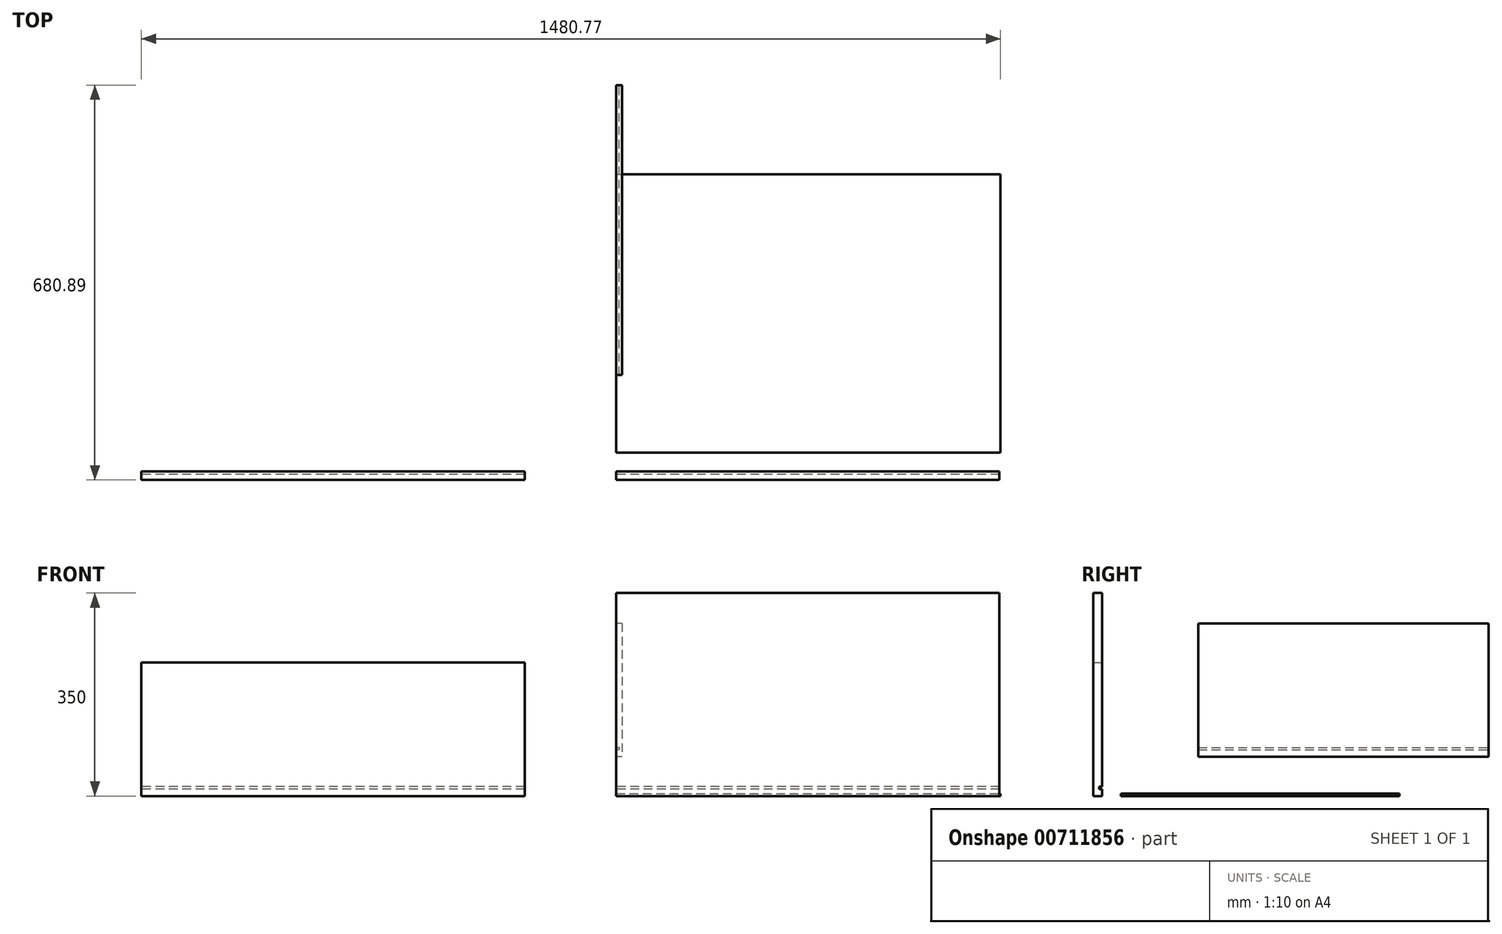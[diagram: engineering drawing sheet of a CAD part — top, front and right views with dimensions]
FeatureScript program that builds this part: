
annotation { "Feature Type Name" : "Feature", "Feature Type Description" : "" }
export const myFeature = defineFeature(function(context is Context, id is Id, definition is map)
    precondition{}
    {
        {
            var Q0;
            Q0=qCreatedBy(makeId("Front.planeOp"),FACE);
            var sketch = newSketch(context, id + "F0", { "sketchPlane" : qUnion([Q0])});
            skLineSegment(sketch, "E0.bottom", {"start": v(0, 0) * mm, "end": v(660.5, 0) * mm});
            skLineSegment(sketch, "E0.top", {"start": v(0, 350) * mm, "end": v(660.5, 350) * mm});
            skLineSegment(sketch, "E0.left", {"start": v(0, 0) * mm, "end": v(0, 350) * mm});
            skLineSegment(sketch, "E0.right", {"start": v(660.5, 0) * mm, "end": v(660.5, 350) * mm});
            skLineSegment(sketch, "E1.bottom", {"start": v(660.5, 16) * mm, "end": v(0, 16) * mm});
            skLineSegment(sketch, "E1.top", {"start": v(660.5, 12) * mm, "end": v(0, 12) * mm});
            skLineSegment(sketch, "E1.left", {"start": v(660.5, 16) * mm, "end": v(660.5, 12) * mm});
            skLineSegment(sketch, "E1.right", {"start": v(0, 16) * mm, "end": v(0, 12) * mm});
            skSolve(sketch);
        }
        {
            var Q0;
            Q0 = qSketchRegion(id + "F0", true);
            extrude(context, id + "F1", {"entities" : qUnion([Q0]), "depth" : 15 * mm, "offsetDistance" : 25 * mm});
        }
        {
            var Q0;
            Q0=qCreatedBy(makeId("Top.planeOp"),FACE);
            var sketch = newSketch(context, id + "F2", { "sketchPlane" : qUnion([Q0])});
            skLineSegment(sketch, "E2.bottom", {"start": v(0, 32.48) * mm, "end": v(662.5, 32.48) * mm});
            skLineSegment(sketch, "E2.top", {"start": v(0, 512.48) * mm, "end": v(662.5, 512.48) * mm});
            skLineSegment(sketch, "E2.left", {"start": v(0, 32.48) * mm, "end": v(0, 512.48) * mm});
            skLineSegment(sketch, "E2.right", {"start": v(662.5, 32.48) * mm, "end": v(662.5, 512.48) * mm});
            skSolve(sketch);
        }
        {
            var Q0;
            Q0 = qSketchRegion(id + "F2", true);
            extrude(context, id + "F3", {"entities" : qUnion([Q0]), "depth" : 4 * mm, "offsetDistance" : 25 * mm});
        }
        {
            var Q0;
            Q0=makeQuery(id+"F0.imprint","IMPRINT",FACE,{"disambiguationData":[TD([[makeQuery(id+"F0.imprint","IMPRINT",EDGE,{"derivedFrom":sQuery(id+"F0.wireOp",EDGE,"E1.bottom")}),1.0]])]});
            extrude(context, id + "F4", {"entities" : qUnion([Q0]), "operationType" : NewBodyOperationType.REMOVE, "depth" : 5 * mm, "offsetDistance" : 25 * mm});
        }
        {
            var Q0;
            Q0=qCreatedBy(makeId("Front.planeOp"),FACE);
            var sketch = newSketch(context, id + "F5", { "sketchPlane" : qUnion([Q0])});
            skLineSegment(sketch, "E3.bottom", {"start": v(-157.77, 230) * mm, "end": v(-818.27, 230) * mm});
            skLineSegment(sketch, "E3.top", {"start": v(-157.77, 0) * mm, "end": v(-818.27, 0) * mm});
            skLineSegment(sketch, "E3.left", {"start": v(-157.77, 230) * mm, "end": v(-157.77, 0) * mm});
            skLineSegment(sketch, "E3.right", {"start": v(-818.27, 230) * mm, "end": v(-818.27, 0) * mm});
            skLineSegment(sketch, "E4.bottom", {"start": v(-157.77, 16) * mm, "end": v(-818.27, 16) * mm});
            skLineSegment(sketch, "E4.top", {"start": v(-157.77, 12) * mm, "end": v(-818.27, 12) * mm});
            skLineSegment(sketch, "E4.left", {"start": v(-157.77, 16) * mm, "end": v(-157.77, 12) * mm});
            skLineSegment(sketch, "E4.right", {"start": v(-818.27, 16) * mm, "end": v(-818.27, 12) * mm});
            skSolve(sketch);
        }
        {
            var Q0;
            {var subQ0=sQuery(id+"F5.wireOp",EDGE,"E3.bottom");Q0=makeQuery(id+"F5.imprint","IMPRINT",FACE,{"disambiguationData":[TD([[makeQuery(id+"F5.imprint","IMPRINT",EDGE,{"derivedFrom":subQ0}),1.0]])]});}
            var Q1;
            Q1=makeQuery(id+"F5.imprint","IMPRINT",FACE,{"disambiguationData":[TD([[makeQuery(id+"F5.imprint","IMPRINT",EDGE,{"derivedFrom":sQuery(id+"F5.wireOp",EDGE,"E4.bottom")}),1.0]])]});
            var Q2;
            {var subQ0=sQuery(id+"F5.wireOp",EDGE,"E3.top");Q2=makeQuery(id+"F5.imprint","IMPRINT",FACE,{"disambiguationData":[TD([[makeQuery(id+"F5.imprint","IMPRINT",EDGE,{"derivedFrom":subQ0}),-1.0]])]});}
            extrude(context, id + "F6", {"entities" : qUnion([Q0, Q1, Q2]), "depth" : 15 * mm, "offsetDistance" : 25 * mm});
        }
        {
            var Q0;
            Q0=makeQuery(id+"F5.imprint","IMPRINT",FACE,{"disambiguationData":[TD([[makeQuery(id+"F5.imprint","IMPRINT",EDGE,{"derivedFrom":sQuery(id+"F5.wireOp",EDGE,"E4.bottom")}),1.0]])]});
            extrude(context, id + "F7", {"entities" : qUnion([Q0]), "operationType" : NewBodyOperationType.REMOVE, "depth" : 5 * mm, "offsetDistance" : 25 * mm});
        }
        {
            var Q0;
            Q0=qCreatedBy(makeId("Right.planeOp"),FACE);
            var sketch = newSketch(context, id + "F8", { "sketchPlane" : qUnion([Q0])});
            skLineSegment(sketch, "E5.bottom", {"start": v(165.9, 297.75) * mm, "end": v(665.9, 297.75) * mm});
            skLineSegment(sketch, "E5.top", {"start": v(165.9, 67.75) * mm, "end": v(665.9, 67.75) * mm});
            skLineSegment(sketch, "E5.left", {"start": v(165.9, 297.75) * mm, "end": v(165.9, 67.75) * mm});
            skLineSegment(sketch, "E5.right", {"start": v(665.9, 297.75) * mm, "end": v(665.9, 67.75) * mm});
            skLineSegment(sketch, "E6.bottom", {"start": v(165.9, 79.75) * mm, "end": v(665.9, 79.75) * mm});
            skLineSegment(sketch, "E6.top", {"start": v(165.9, 83.75) * mm, "end": v(665.9, 83.75) * mm});
            skLineSegment(sketch, "E6.left", {"start": v(165.9, 79.75) * mm, "end": v(165.9, 83.75) * mm});
            skLineSegment(sketch, "E6.right", {"start": v(665.9, 79.75) * mm, "end": v(665.9, 83.75) * mm});
            skSolve(sketch);
        }
        {
            var Q0;
            {var subQ0=sQuery(id+"F8.wireOp",EDGE,"E5.bottom");Q0=makeQuery(id+"F8.imprint","IMPRINT",FACE,{"disambiguationData":[TD([[makeQuery(id+"F8.imprint","IMPRINT",EDGE,{"derivedFrom":subQ0}),-1.0]])]});}
            var Q1;
            Q1=makeQuery(id+"F8.imprint","IMPRINT",FACE,{"disambiguationData":[TD([[makeQuery(id+"F8.imprint","IMPRINT",EDGE,{"derivedFrom":sQuery(id+"F8.wireOp",EDGE,"E6.bottom")}),1.0]])]});
            var Q2;
            {var subQ0=sQuery(id+"F8.wireOp",EDGE,"E5.top");Q2=makeQuery(id+"F8.imprint","IMPRINT",FACE,{"disambiguationData":[TD([[makeQuery(id+"F8.imprint","IMPRINT",EDGE,{"derivedFrom":subQ0}),1.0]])]});}
            extrude(context, id + "F9", {"entities" : qUnion([Q0, Q1, Q2]), "depth" : 10 * mm, "offsetDistance" : 25 * mm});
        }
        {
            var Q0;
            Q0=makeQuery(id+"F8.imprint","IMPRINT",FACE,{"disambiguationData":[TD([[makeQuery(id+"F8.imprint","IMPRINT",EDGE,{"derivedFrom":sQuery(id+"F8.wireOp",EDGE,"E6.bottom")}),1.0]])]});
            extrude(context, id + "F10", {"entities" : qUnion([Q0]), "operationType" : NewBodyOperationType.REMOVE, "depth" : 5 * mm, "offsetDistance" : 25 * mm});
        }
    });
